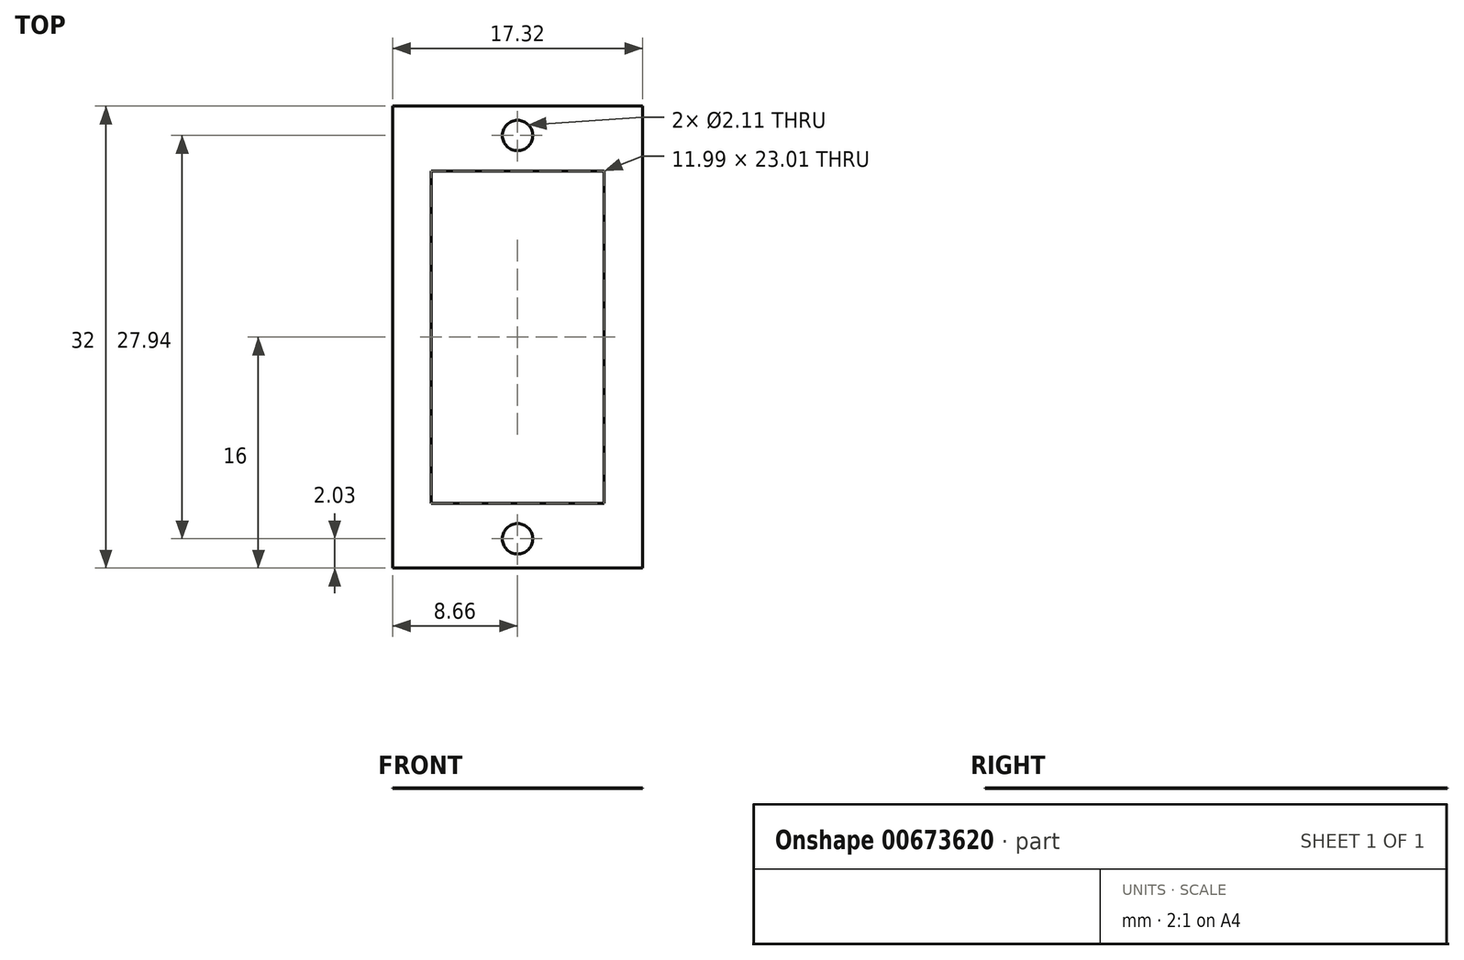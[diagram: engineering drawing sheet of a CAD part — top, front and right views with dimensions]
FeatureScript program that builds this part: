
annotation { "Feature Type Name" : "Feature", "Feature Type Description" : "" }
export const myFeature = defineFeature(function(context is Context, id is Id, definition is map)
    precondition{}
    {
        {
            var Q0;
            Q0=qCreatedBy(makeId("Top.planeOp"),FACE);
            var sketch = newSketch(context, id + "F0", { "sketchPlane" : qUnion([Q0])});
            skLineSegment(sketch, "E0.bottom", {"start": v(8.66, -16) * mm, "end": v(-8.66, -16) * mm});
            skLineSegment(sketch, "E0.top", {"start": v(8.66, 16) * mm, "end": v(-8.66, 16) * mm});
            skLineSegment(sketch, "E0.left", {"start": v(8.66, -16) * mm, "end": v(8.66, 16) * mm});
            skLineSegment(sketch, "E0.right", {"start": v(-8.66, -16) * mm, "end": v(-8.66, 16) * mm});
            skPoint(sketch, "E0.middle", {"position": v(0, 0) * mm});
            skLineSegment(sketch, "E1.bottom", {"start": v(6, -11.5) * mm, "end": v(-6, -11.5) * mm});
            skLineSegment(sketch, "E1.top", {"start": v(6, 11.5) * mm, "end": v(-6, 11.5) * mm});
            skLineSegment(sketch, "E1.left", {"start": v(6, -11.5) * mm, "end": v(6, 11.5) * mm});
            skLineSegment(sketch, "E1.right", {"start": v(-6, -11.5) * mm, "end": v(-6, 11.5) * mm});
            skCircle(sketch, "E2", {"center": v(0, 13.97) * mm, "radius": 1.05 * mm});
            skCircle(sketch, "E3", {"center": v(0, -13.97) * mm, "radius": 1.05 * mm});
            skLineSegment(sketch, "E4", {"start": v(0, 13.97) * mm, "end": v(0, 11.5) * mm, "construction": true});
            skLineSegment(sketch, "E5", {"start": v(0, -13.97) * mm, "end": v(0, -11.5) * mm, "construction": true});
            skSolve(sketch);
        }
        {
            var Q0;
            Q0=makeQuery(id+"F0.imprint","IMPRINT",FACE,{"disambiguationData":[TD([[makeQuery(id+"F0.imprint","IMPRINT",EDGE,{"derivedFrom":sQuery(id+"F0.wireOp",EDGE,"E0.bottom")}),-1.0]])]});
            extrude(context, id + "F1", {"entities" : qUnion([Q0]), "depth" : 1 / 203.2 * mm});
        }
    });
